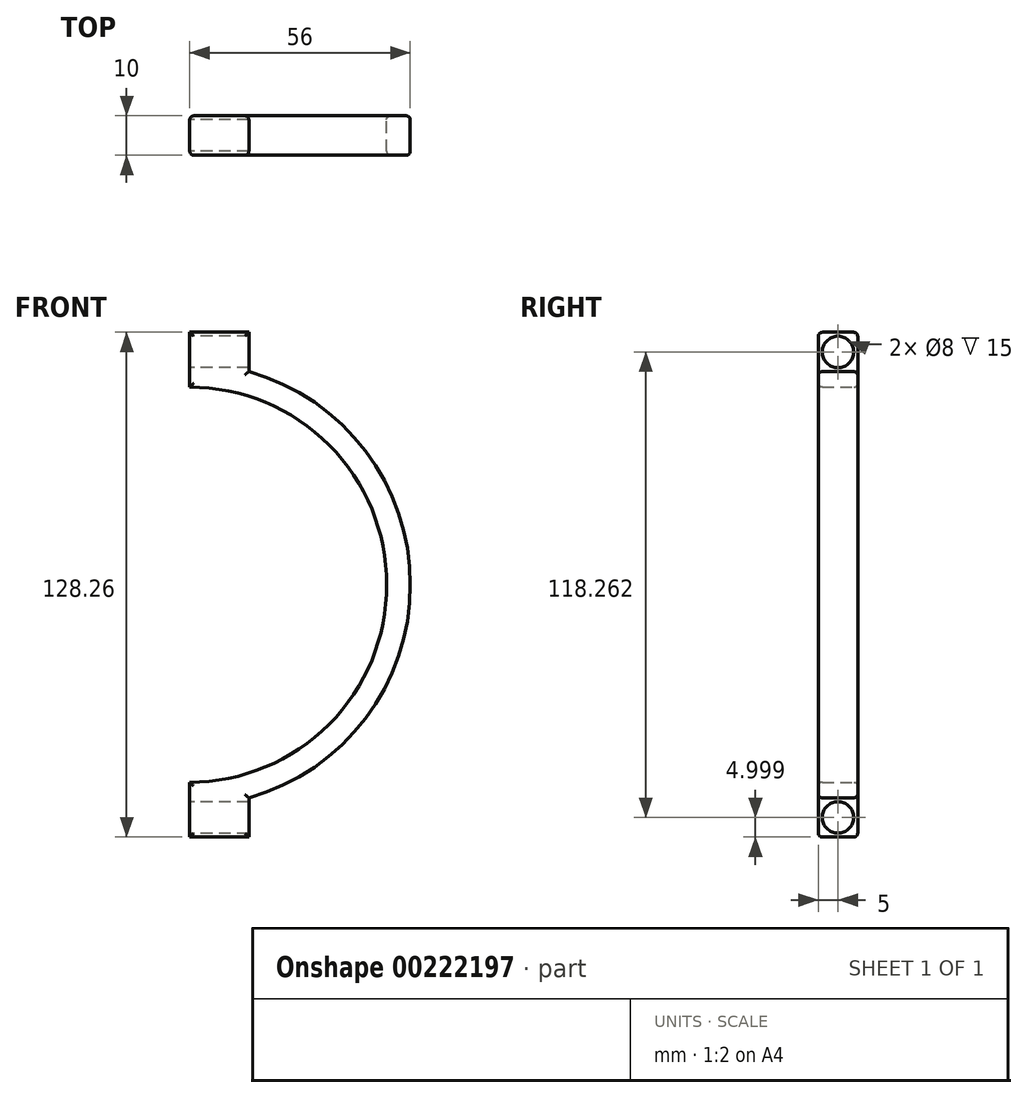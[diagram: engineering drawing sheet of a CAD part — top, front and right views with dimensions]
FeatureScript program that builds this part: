
annotation { "Feature Type Name" : "Feature", "Feature Type Description" : "" }
export const myFeature = defineFeature(function(context is Context, id is Id, definition is map)
    precondition{}
    {
        {
            var Q0;
            Q0=qCreatedBy(makeId("Front.planeOp"),FACE);
            var sketch = newSketch(context, id + "F0", { "sketchPlane" : qUnion([Q0])});
            skArc(sketch, "E0", {"start": v(50, 0) * mm, "mid": v(35.42, 35.47) * mm, "end": v(0, 50.18) * mm});
            skLineSegment(sketch, "E1", {"start": v(0, 50.18) * mm, "end": v(0, 64.13) * mm});
            skLineSegment(sketch, "E2", {"start": v(0, 64.13) * mm, "end": v(15, 64.13) * mm});
            skArc(sketch, "E3.0", {"start": v(56, 0) * mm, "mid": v(44.64, 33.99) * mm, "end": v(15, 54.13) * mm});
            skLineSegment(sketch, "E4", {"start": v(15, 64.13) * mm, "end": v(15, 54.13) * mm});
            skPoint(sketch, "E5.orphan", {"position": v(0, -49.82) * mm});
            skArc(sketch, "E6.MirrorCS", {"start": v(50, 0) * mm, "mid": v(35.42, -35.47) * mm, "end": v(0, -50.18) * mm});
            skLineSegment(sketch, "E7.MirrorCS", {"start": v(15, -64.13) * mm, "end": v(15, -54.13) * mm});
            skLineSegment(sketch, "E8.MirrorCS", {"start": v(0, -50.18) * mm, "end": v(0, -64.13) * mm});
            skArc(sketch, "E9.MirrorCS", {"start": v(56, 0) * mm, "mid": v(44.64, -33.99) * mm, "end": v(15, -54.13) * mm});
            skLineSegment(sketch, "E10.MirrorCS", {"start": v(0, -64.13) * mm, "end": v(15, -64.13) * mm});
            skSolve(sketch);
        }
        {
            var Q0;
            Q0=makeQuery(id+"F0.imprint","IMPRINT",FACE,{"disambiguationData":[TD([[makeQuery(id+"F0.imprint","IMPRINT",EDGE,{"derivedFrom":sQuery(id+"F0.wireOp",EDGE,"E0")}),-1.0]])]});
            extrude(context, id + "F1", {"entities" : qUnion([Q0]), "depth" : 10 * mm});
        }
        {
            var Q0;
            Q0=qCreatedBy(makeId("Right.planeOp"),FACE);
            var sketch = newSketch(context, id + "F2", { "sketchPlane" : qUnion([Q0])});
            skPoint(sketch, "E11", {"position": v(-5, 59.13) * mm});
            skPoint(sketch, "E12", {"position": v(-5, -59.13) * mm});
            skSolve(sketch);
        }
        {
            var Q0;
            Q0=sQuery(id+"F2.wireOp",VERTEX,"E11");
            var Q1;
            Q1=sQuery(id+"F2.wireOp",VERTEX,"E12");
            var Q2;
            Q2=makeQuery(id+"F1.opExtrude","SWEPT_BODY",BODY,{"disambiguationData":[OSD([sQuery(id+"F0.wireOp",EDGE,"E0"),sQuery(id+"F0.wireOp",EDGE,"E1"),sQuery(id+"F0.wireOp",EDGE,"E2"),sQuery(id+"F0.wireOp",EDGE,"E3.0"),sQuery(id+"F0.wireOp",EDGE,"E4"),sQuery(id+"F0.wireOp",EDGE,"E6.MirrorCS"),sQuery(id+"F0.wireOp",EDGE,"E7.MirrorCS"),sQuery(id+"F0.wireOp",EDGE,"E8.MirrorCS"),sQuery(id+"F0.wireOp",EDGE,"E9.MirrorCS"),sQuery(id+"F0.wireOp",EDGE,"E10.MirrorCS")])]});
            hole(context, id + "F3", {"style" : HoleStyle.SIMPLE, "endStyle" : HoleEndStyle.THROUGH, "oppositeDirection" : true, "holeDiameter" : 8 * mm, "locations" : qUnion([Q0, Q1]), "scope" : qUnion([Q2]), "isTappedThrough" : true});
        }
        {
            var Q0;
            Q0=makeQuery(id+"F1.opExtrude","CAP_FACE",FACE,{"disambiguationData":[OSD([sQuery(id+"F0.wireOp",EDGE,"E0"),sQuery(id+"F0.wireOp",EDGE,"E1"),sQuery(id+"F0.wireOp",EDGE,"E2"),sQuery(id+"F0.wireOp",EDGE,"E3.0"),sQuery(id+"F0.wireOp",EDGE,"E4"),sQuery(id+"F0.wireOp",EDGE,"E6.MirrorCS"),sQuery(id+"F0.wireOp",EDGE,"E7.MirrorCS"),sQuery(id+"F0.wireOp",EDGE,"E8.MirrorCS"),sQuery(id+"F0.wireOp",EDGE,"E9.MirrorCS"),sQuery(id+"F0.wireOp",EDGE,"E10.MirrorCS")])],"isStart":false});
            fillet(context, id + "F4", {"entities" : qUnion([Q0]), "radius" : 1 * mm, "tangentPropagation" : true, "allowEdgeOverflow" : false});
        }
        {
            var Q0;
            Q0=makeQuery(id+"F1.opExtrude","CAP_FACE",FACE,{"disambiguationData":[OSD([sQuery(id+"F0.wireOp",EDGE,"E0"),sQuery(id+"F0.wireOp",EDGE,"E1"),sQuery(id+"F0.wireOp",EDGE,"E2"),sQuery(id+"F0.wireOp",EDGE,"E3.0"),sQuery(id+"F0.wireOp",EDGE,"E4"),sQuery(id+"F0.wireOp",EDGE,"E6.MirrorCS"),sQuery(id+"F0.wireOp",EDGE,"E7.MirrorCS"),sQuery(id+"F0.wireOp",EDGE,"E8.MirrorCS"),sQuery(id+"F0.wireOp",EDGE,"E9.MirrorCS"),sQuery(id+"F0.wireOp",EDGE,"E10.MirrorCS")])],"isStart":true});
            fillet(context, id + "F5", {"entities" : qUnion([Q0]), "radius" : 1 * mm, "tangentPropagation" : true, "allowEdgeOverflow" : false});
        }
    });
